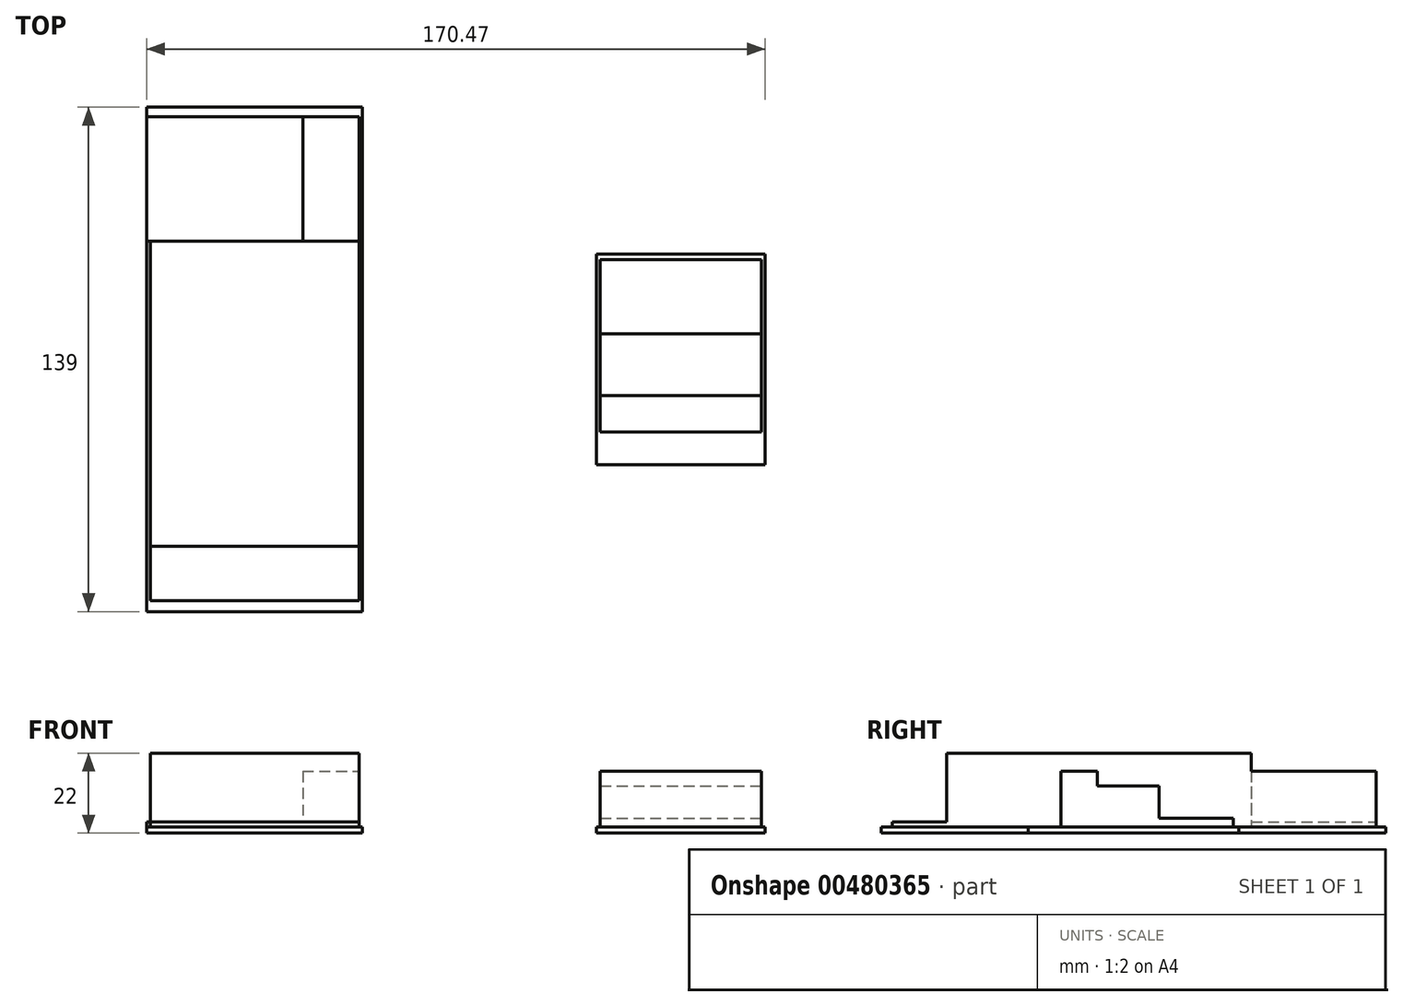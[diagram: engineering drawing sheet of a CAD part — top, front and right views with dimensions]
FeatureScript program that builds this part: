
annotation { "Feature Type Name" : "Feature", "Feature Type Description" : "" }
export const myFeature = defineFeature(function(context is Context, id is Id, definition is map)
    precondition{}
    {
        {
            var Q0;
            Q0=qCreatedBy(makeId("Top.planeOp"),FACE);
            var sketch = newSketch(context, id + "F0", { "sketchPlane" : qUnion([Q0])});
            skLineSegment(sketch, "E0.bottom", {"start": v(-45.08, -69.5) * mm, "end": v(-104.58, -69.5) * mm});
            skLineSegment(sketch, "E0.top", {"start": v(-45.08, 69.5) * mm, "end": v(-104.58, 69.5) * mm});
            skLineSegment(sketch, "E0.left", {"start": v(-45.08, -69.5) * mm, "end": v(-45.08, 69.5) * mm});
            skLineSegment(sketch, "E0.right", {"start": v(-104.58, -69.5) * mm, "end": v(-104.58, 69.5) * mm});
            skPoint(sketch, "E0.middle", {"position": v(-74.83, 0) * mm});
            skLineSegment(sketch, "E1.bottom", {"start": v(65.9, -29) * mm, "end": v(19.4, -29) * mm});
            skLineSegment(sketch, "E1.top", {"start": v(65.9, 29) * mm, "end": v(19.4, 29) * mm});
            skLineSegment(sketch, "E1.left", {"start": v(65.9, -29) * mm, "end": v(65.9, 29) * mm});
            skLineSegment(sketch, "E1.right", {"start": v(19.4, -29) * mm, "end": v(19.4, 29) * mm});
            skPoint(sketch, "E1.middle", {"position": v(42.64, 0) * mm});
            skLineSegment(sketch, "E2.bottom", {"start": v(19.4, -10) * mm, "end": v(65.9, -10) * mm});
            skLineSegment(sketch, "E2.top", {"start": v(19.4, -20) * mm, "end": v(65.9, -20) * mm});
            skLineSegment(sketch, "E3.top", {"start": v(19.4, 7) * mm, "end": v(65.9, 7) * mm});
            skLineSegment(sketch, "E4", {"start": v(19.4, 27.5) * mm, "end": v(65.9, 27.5) * mm});
            skLineSegment(sketch, "E5", {"start": v(-104.58, -66.5) * mm, "end": v(-45.08, -66.5) * mm});
            skLineSegment(sketch, "E6", {"start": v(-104.58, -51.5) * mm, "end": v(-45.08, -51.5) * mm});
            skLineSegment(sketch, "E7", {"start": v(-104.58, 32.5) * mm, "end": v(-45.08, 32.5) * mm});
            skLineSegment(sketch, "E8", {"start": v(-104.58, 66.9) * mm, "end": v(-45.08, 66.9) * mm});
            skLineSegment(sketch, "E9", {"start": v(-61.58, 32.5) * mm, "end": v(-61.58, 66.9) * mm});
            skLineSegment(sketch, "E10", {"start": v(20.4, 29) * mm, "end": v(20.4, -29) * mm});
            skLineSegment(sketch, "E11", {"start": v(64.9, 29) * mm, "end": v(64.9, -29) * mm});
            skLineSegment(sketch, "E12", {"start": v(-103.58, 69.5) * mm, "end": v(-103.58, -69.5) * mm});
            skLineSegment(sketch, "E13", {"start": v(-46.08, 69.5) * mm, "end": v(-46.08, -69.5) * mm});
            skSolve(sketch);
        }
        {
            var Q0;
            {var subQ4=sQuery(id+"F0.wireOp",EDGE,"E0.top");Q0=makeQuery(id+"F0.imprint","IMPRINT",FACE,{"disambiguationData":[TD([[makeQuery(id+"F0.imprint","IMPRINT",EDGE,{"derivedFrom":subQ4}),1.0]])]});}
            var Q1;
            {var subQ0=sQuery(id+"F0.wireOp",EDGE,"E0.bottom");Q1=makeQuery(id+"F0.imprint","IMPRINT",FACE,{"disambiguationData":[TD([[makeQuery(id+"F0.imprint","IMPRINT",EDGE,{"derivedFrom":subQ0}),-1.0]])]});}
            var Q2;
            {var subQ0=sQuery(id+"F0.wireOp",EDGE,"E1.top");Q2=makeQuery(id+"F0.imprint","IMPRINT",FACE,{"disambiguationData":[TD([[makeQuery(id+"F0.imprint","IMPRINT",EDGE,{"derivedFrom":subQ0}),1.0]])]});}
            var Q3;
            {var subQ0=sQuery(id+"F0.wireOp",EDGE,"E1.bottom");Q3=makeQuery(id+"F0.imprint","IMPRINT",FACE,{"disambiguationData":[TD([[makeQuery(id+"F0.imprint","IMPRINT",EDGE,{"derivedFrom":subQ0}),-1.0]])]});}
            var Q4;
            {var subQ0=sQuery(id+"F0.wireOp",EDGE,"E3.top");var subQ1=sQuery(id+"F0.wireOp",EDGE,"E1.right");var subQ2=makeQuery(id+"F0.imprint","INTERSECT",VERTEX,{"derivedFrom":[subQ1,subQ0]});Q4=makeQuery(id+"F0.imprint","IMPRINT",FACE,{"disambiguationData":[TD([[makeQuery(id+"F0.imprint","IMPRINT",EDGE,{"disambiguationData":[TD([[subQ2,-1.0]])],"derivedFrom":subQ1}),-1.0]])]});}
            var Q5;
            {var subQ0=sQuery(id+"F0.wireOp",EDGE,"E2.bottom");var subQ1=sQuery(id+"F0.wireOp",EDGE,"E1.right");var subQ2=makeQuery(id+"F0.imprint","INTERSECT",VERTEX,{"derivedFrom":[subQ1,subQ0]});Q5=makeQuery(id+"F0.imprint","IMPRINT",FACE,{"disambiguationData":[TD([[makeQuery(id+"F0.imprint","IMPRINT",EDGE,{"disambiguationData":[TD([[subQ2,-1.0]])],"derivedFrom":subQ1}),-1.0]])]});}
            var Q6;
            {var subQ0=sQuery(id+"F0.wireOp",EDGE,"E2.top");var subQ1=sQuery(id+"F0.wireOp",EDGE,"E1.right");var subQ2=makeQuery(id+"F0.imprint","INTERSECT",VERTEX,{"derivedFrom":[subQ1,subQ0]});Q6=makeQuery(id+"F0.imprint","IMPRINT",FACE,{"disambiguationData":[TD([[makeQuery(id+"F0.imprint","IMPRINT",EDGE,{"disambiguationData":[TD([[subQ2,-1.0]])],"derivedFrom":subQ1}),-1.0]])]});}
            var Q7;
            {var subQ0=sQuery(id+"F0.wireOp",EDGE,"E2.top");var subQ1=sQuery(id+"F0.wireOp",EDGE,"E1.left");var subQ2=makeQuery(id+"F0.imprint","INTERSECT",VERTEX,{"derivedFrom":[subQ1,subQ0]});Q7=makeQuery(id+"F0.imprint","IMPRINT",FACE,{"disambiguationData":[TD([[makeQuery(id+"F0.imprint","IMPRINT",EDGE,{"disambiguationData":[TD([[subQ2,-1.0]])],"derivedFrom":subQ1}),1.0]])]});}
            var Q8;
            {var subQ0=sQuery(id+"F0.wireOp",EDGE,"E2.bottom");var subQ1=sQuery(id+"F0.wireOp",EDGE,"E1.left");var subQ2=makeQuery(id+"F0.imprint","INTERSECT",VERTEX,{"derivedFrom":[subQ1,subQ0]});Q8=makeQuery(id+"F0.imprint","IMPRINT",FACE,{"disambiguationData":[TD([[makeQuery(id+"F0.imprint","IMPRINT",EDGE,{"disambiguationData":[TD([[subQ2,-1.0]])],"derivedFrom":subQ1}),1.0]])]});}
            var Q9;
            {var subQ0=sQuery(id+"F0.wireOp",EDGE,"E3.top");var subQ1=sQuery(id+"F0.wireOp",EDGE,"E1.left");var subQ2=makeQuery(id+"F0.imprint","INTERSECT",VERTEX,{"derivedFrom":[subQ1,subQ0]});Q9=makeQuery(id+"F0.imprint","IMPRINT",FACE,{"disambiguationData":[TD([[makeQuery(id+"F0.imprint","IMPRINT",EDGE,{"disambiguationData":[TD([[subQ2,-1.0]])],"derivedFrom":subQ1}),1.0]])]});}
            var Q10;
            {var subQ0=sQuery(id+"F0.wireOp",EDGE,"E6");var subQ1=sQuery(id+"F0.wireOp",EDGE,"E0.right");var subQ2=makeQuery(id+"F0.imprint","INTERSECT",VERTEX,{"derivedFrom":[subQ1,subQ0]});Q10=makeQuery(id+"F0.imprint","IMPRINT",FACE,{"disambiguationData":[TD([[makeQuery(id+"F0.imprint","IMPRINT",EDGE,{"disambiguationData":[TD([[subQ2,-1.0]])],"derivedFrom":subQ1}),-1.0]])]});}
            var Q11;
            {var subQ0=sQuery(id+"F0.wireOp",EDGE,"E5");var subQ1=sQuery(id+"F0.wireOp",EDGE,"E0.right");var subQ2=makeQuery(id+"F0.imprint","INTERSECT",VERTEX,{"derivedFrom":[subQ1,subQ0]});Q11=makeQuery(id+"F0.imprint","IMPRINT",FACE,{"disambiguationData":[TD([[makeQuery(id+"F0.imprint","IMPRINT",EDGE,{"disambiguationData":[TD([[subQ2,-1.0]])],"derivedFrom":subQ1}),-1.0]])]});}
            var Q12;
            {var subQ0=sQuery(id+"F0.wireOp",EDGE,"E5");var subQ1=sQuery(id+"F0.wireOp",EDGE,"E0.left");var subQ2=makeQuery(id+"F0.imprint","INTERSECT",VERTEX,{"derivedFrom":[subQ1,subQ0]});Q12=makeQuery(id+"F0.imprint","IMPRINT",FACE,{"disambiguationData":[TD([[makeQuery(id+"F0.imprint","IMPRINT",EDGE,{"disambiguationData":[TD([[subQ2,-1.0]])],"derivedFrom":subQ1}),1.0]])]});}
            var Q13;
            {var subQ0=sQuery(id+"F0.wireOp",EDGE,"E6");var subQ1=sQuery(id+"F0.wireOp",EDGE,"E0.left");var subQ2=makeQuery(id+"F0.imprint","INTERSECT",VERTEX,{"derivedFrom":[subQ1,subQ0]});Q13=makeQuery(id+"F0.imprint","IMPRINT",FACE,{"disambiguationData":[TD([[makeQuery(id+"F0.imprint","IMPRINT",EDGE,{"disambiguationData":[TD([[subQ2,-1.0]])],"derivedFrom":subQ1}),1.0]])]});}
            var Q14;
            {var subQ0=sQuery(id+"F0.wireOp",EDGE,"E7");var subQ1=sQuery(id+"F0.wireOp",EDGE,"E0.left");var subQ2=makeQuery(id+"F0.imprint","INTERSECT",VERTEX,{"derivedFrom":[subQ1,subQ0]});Q14=makeQuery(id+"F0.imprint","IMPRINT",FACE,{"disambiguationData":[TD([[makeQuery(id+"F0.imprint","IMPRINT",EDGE,{"disambiguationData":[TD([[subQ2,-1.0]])],"derivedFrom":subQ1}),1.0]])]});}
            var Q15;
            {var subQ4=sQuery(id+"F0.wireOp",EDGE,"E12");var subQ6=sQuery(id+"F0.wireOp",EDGE,"E0.top");var subQ7=makeQuery(id+"F0.imprint","INTERSECT",VERTEX,{"derivedFrom":[subQ6,subQ4]});Q15=makeQuery(id+"F0.imprint","IMPRINT",FACE,{"disambiguationData":[TD([[makeQuery(id+"F0.imprint","IMPRINT",EDGE,{"disambiguationData":[TD([[subQ7,1.0]])],"derivedFrom":subQ6}),1.0]])]});}
            extrude(context, id + "F1", {"entities" : qUnion([Q0, Q1, Q2, Q3, Q4, Q5, Q6, Q7, Q8, Q9, Q10, Q11, Q12, Q13, Q14, Q15]), "depth" : 1.6 * mm, "offsetDistance" : 25 * mm});
        }
        {
            var Q0;
            {var subQ0=sQuery(id+"F0.wireOp",EDGE,"E12");var subQ1=sQuery(id+"F0.wireOp",EDGE,"E5");var subQ2=makeQuery(id+"F0.imprint","INTERSECT",VERTEX,{"derivedFrom":[subQ1,subQ0]});Q0=makeQuery(id+"F0.imprint","IMPRINT",FACE,{"disambiguationData":[TD([[makeQuery(id+"F0.imprint","IMPRINT",EDGE,{"disambiguationData":[TD([[subQ2,-1.0]])],"derivedFrom":subQ1}),1.0]])]});}
            var Q1;
            {var subQ0=sQuery(id+"F0.wireOp",EDGE,"E7");var subQ1=sQuery(id+"F0.wireOp",EDGE,"E0.right");var subQ2=makeQuery(id+"F0.imprint","INTERSECT",VERTEX,{"derivedFrom":[subQ1,subQ0]});Q1=makeQuery(id+"F0.imprint","IMPRINT",FACE,{"disambiguationData":[TD([[makeQuery(id+"F0.imprint","IMPRINT",EDGE,{"disambiguationData":[TD([[subQ2,-1.0]])],"derivedFrom":subQ1}),-1.0]])]});}
            var Q2;
            {var subQ0=sQuery(id+"F0.wireOp",EDGE,"E9");Q2=makeQuery(id+"F0.imprint","IMPRINT",FACE,{"disambiguationData":[TD([[makeQuery(id+"F0.imprint","IMPRINT",EDGE,{"derivedFrom":subQ0}),1.0]])]});}
            extrude(context, id + "F2", {"entities" : qUnion([Q0, Q1, Q2]), "operationType" : NewBodyOperationType.ADD, "depth" : 3 * mm, "offsetDistance" : 25 * mm});
        }
        {
            var Q0;
            {var subQ0=sQuery(id+"F0.wireOp",EDGE,"E9");Q0=makeQuery(id+"F0.imprint","IMPRINT",FACE,{"disambiguationData":[TD([[makeQuery(id+"F0.imprint","IMPRINT",EDGE,{"derivedFrom":subQ0}),-1.0]])]});}
            var Q1;
            {var subQ0=sQuery(id+"F0.wireOp",EDGE,"E10");var subQ1=sQuery(id+"F0.wireOp",EDGE,"E2.top");var subQ2=makeQuery(id+"F0.imprint","INTERSECT",VERTEX,{"derivedFrom":[subQ1,subQ0]});Q1=makeQuery(id+"F0.imprint","IMPRINT",FACE,{"disambiguationData":[TD([[makeQuery(id+"F0.imprint","IMPRINT",EDGE,{"disambiguationData":[TD([[subQ2,-1.0]])],"derivedFrom":subQ1}),1.0]])]});}
            extrude(context, id + "F3", {"entities" : qUnion([Q0, Q1]), "operationType" : NewBodyOperationType.ADD, "depth" : 17 * mm, "offsetDistance" : 25 * mm});
        }
        {
            var Q0;
            {var subQ4=sQuery(id+"F0.wireOp",EDGE,"E12");var subQ5=sQuery(id+"F0.wireOp",EDGE,"E6");var subQ6=makeQuery(id+"F0.imprint","INTERSECT",VERTEX,{"derivedFrom":[subQ5,subQ4]});Q0=makeQuery(id+"F0.imprint","IMPRINT",FACE,{"disambiguationData":[TD([[makeQuery(id+"F0.imprint","IMPRINT",EDGE,{"disambiguationData":[TD([[subQ6,-1.0]])],"derivedFrom":subQ5}),1.0]])]});}
            extrude(context, id + "F4", {"entities" : qUnion([Q0]), "operationType" : NewBodyOperationType.ADD, "depth" : 22 * mm, "offsetDistance" : 25 * mm});
        }
        {
            var Q0;
            {var subQ0=sQuery(id+"F0.wireOp",EDGE,"E10");var subQ1=sQuery(id+"F0.wireOp",EDGE,"E3.top");var subQ2=makeQuery(id+"F0.imprint","INTERSECT",VERTEX,{"derivedFrom":[subQ1,subQ0]});Q0=makeQuery(id+"F0.imprint","IMPRINT",FACE,{"disambiguationData":[TD([[makeQuery(id+"F0.imprint","IMPRINT",EDGE,{"disambiguationData":[TD([[subQ2,-1.0]])],"derivedFrom":subQ1}),1.0]])]});}
            extrude(context, id + "F5", {"entities" : qUnion([Q0]), "operationType" : NewBodyOperationType.ADD, "depth" : 4 * mm, "offsetDistance" : 25 * mm});
        }
        {
            var Q0;
            {var subQ0=sQuery(id+"F0.wireOp",EDGE,"E10");var subQ1=sQuery(id+"F0.wireOp",EDGE,"E2.bottom");var subQ2=makeQuery(id+"F0.imprint","INTERSECT",VERTEX,{"derivedFrom":[subQ1,subQ0]});Q0=makeQuery(id+"F0.imprint","IMPRINT",FACE,{"disambiguationData":[TD([[makeQuery(id+"F0.imprint","IMPRINT",EDGE,{"disambiguationData":[TD([[subQ2,-1.0]])],"derivedFrom":subQ1}),1.0]])]});}
            extrude(context, id + "F6", {"entities" : qUnion([Q0]), "operationType" : NewBodyOperationType.ADD, "depth" : 13 * mm, "offsetDistance" : 25 * mm});
        }
    });
